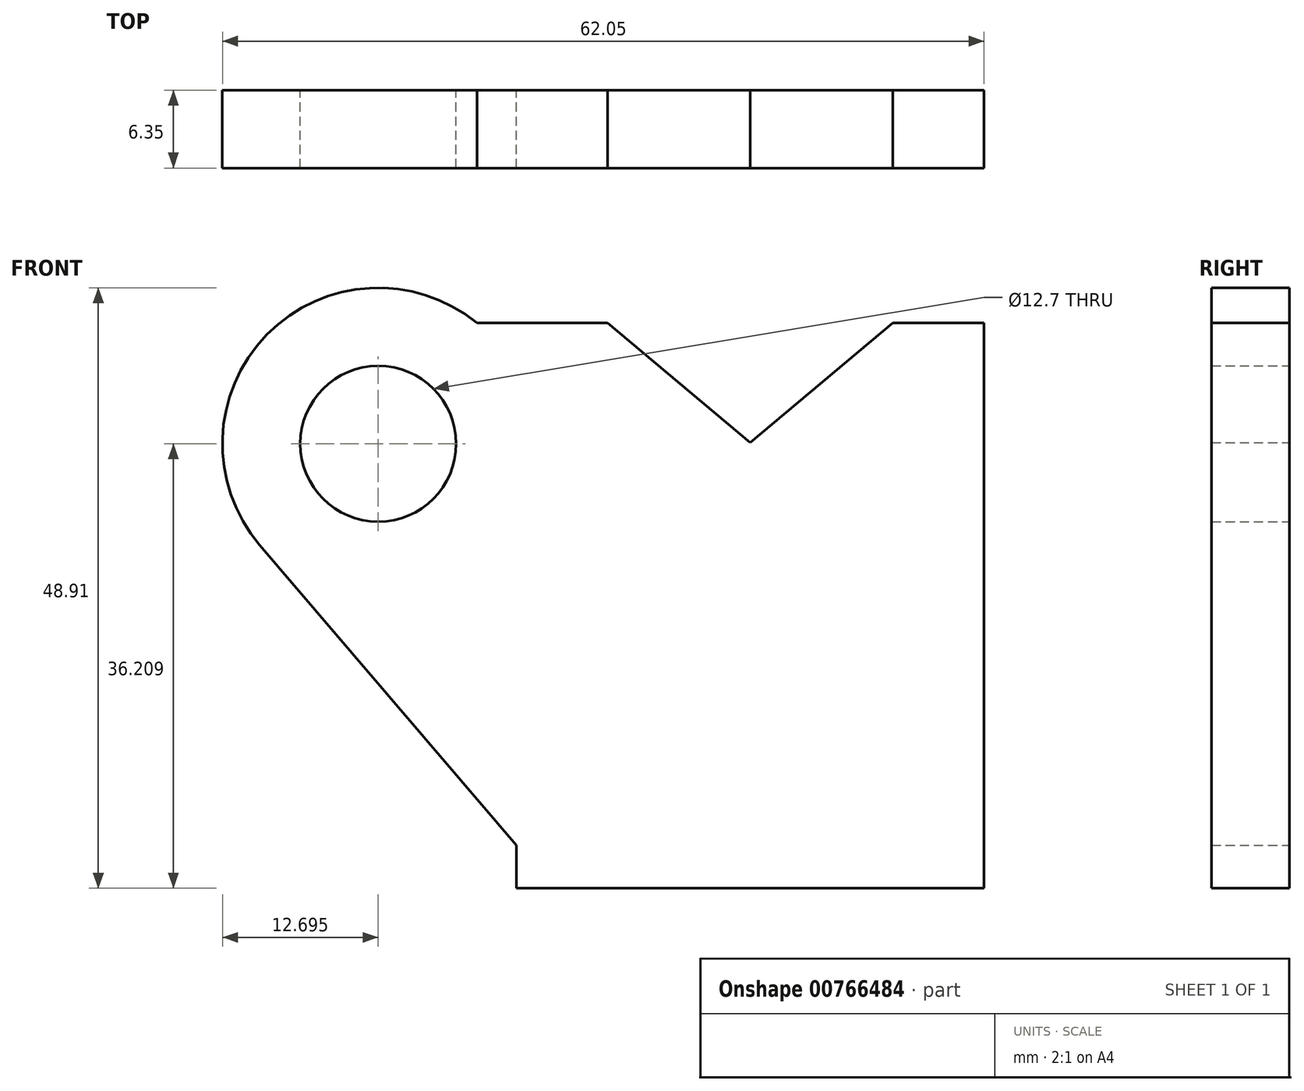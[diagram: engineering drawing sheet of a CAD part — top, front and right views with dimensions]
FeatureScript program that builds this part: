
annotation { "Feature Type Name" : "Feature", "Feature Type Description" : "" }
export const myFeature = defineFeature(function(context is Context, id is Id, definition is map)
    precondition{}
    {
        {
            var Q0;
            Q0=qCreatedBy(makeId("Front.planeOp"),FACE);
            var sketch = newSketch(context, id + "F0", { "sketchPlane" : qUnion([Q0])});
            skCircle(sketch, "E0", {"center": v(-144.03, 58.1) * mm, "radius": 6.35 * mm});
            skArc(sketch, "E1", {"start": v(-136, 67.93) * mm, "mid": v(-153.11, 66.98) * mm, "end": v(-153.69, 49.84) * mm});
            skLineSegment(sketch, "E2", {"start": v(-153.69, 49.84) * mm, "end": v(-132.78, 25.4) * mm});
            skLineSegment(sketch, "E3.trimOffspring", {"start": v(-132.78, 25.4) * mm, "end": v(-132.78, 21.9) * mm});
            skCircle(sketch, "E4", {"center": v(-113.73, 72.7) * mm, "radius": 11.11 * mm, "construction": true});
            skLineSegment(sketch, "E5.0", {"start": v(-136, 67.93) * mm, "end": v(-125.34, 67.93) * mm});
            skLineSegment(sketch, "E6", {"start": v(-94.68, 67.93) * mm, "end": v(-94.68, 21.9) * mm});
            skLineSegment(sketch, "E7.trimOffspring", {"start": v(-102.11, 67.93) * mm, "end": v(-94.68, 67.93) * mm});
            skPoint(sketch, "E8.orphan", {"position": v(-113.73, 54.73) * mm});
            skLineSegment(sketch, "E9.0", {"start": v(-125.34, 67.93) * mm, "end": v(-113.73, 58.19) * mm});
            skLineSegment(sketch, "E10.0", {"start": v(-102.11, 67.93) * mm, "end": v(-113.73, 58.19) * mm});
            skLineSegment(sketch, "E11", {"start": v(-120.87, 64.18) * mm, "end": v(-113.73, 72.7) * mm, "construction": true});
            skLineSegment(sketch, "E12", {"start": v(-106.58, 64.18) * mm, "end": v(-113.73, 72.7) * mm, "construction": true});
            skLineSegment(sketch, "E13.0", {"start": v(-132.78, 21.9) * mm, "end": v(-94.68, 21.9) * mm});
            skSolve(sketch);
        }
        {
            var Q0;
            Q0 = qSketchRegion(id + "F0", true);
            extrude(context, id + "F1", {"entities" : qUnion([Q0]), "depth" : 6.35 * mm, "offsetDistance" : 25.4 * mm});
        }
    });
